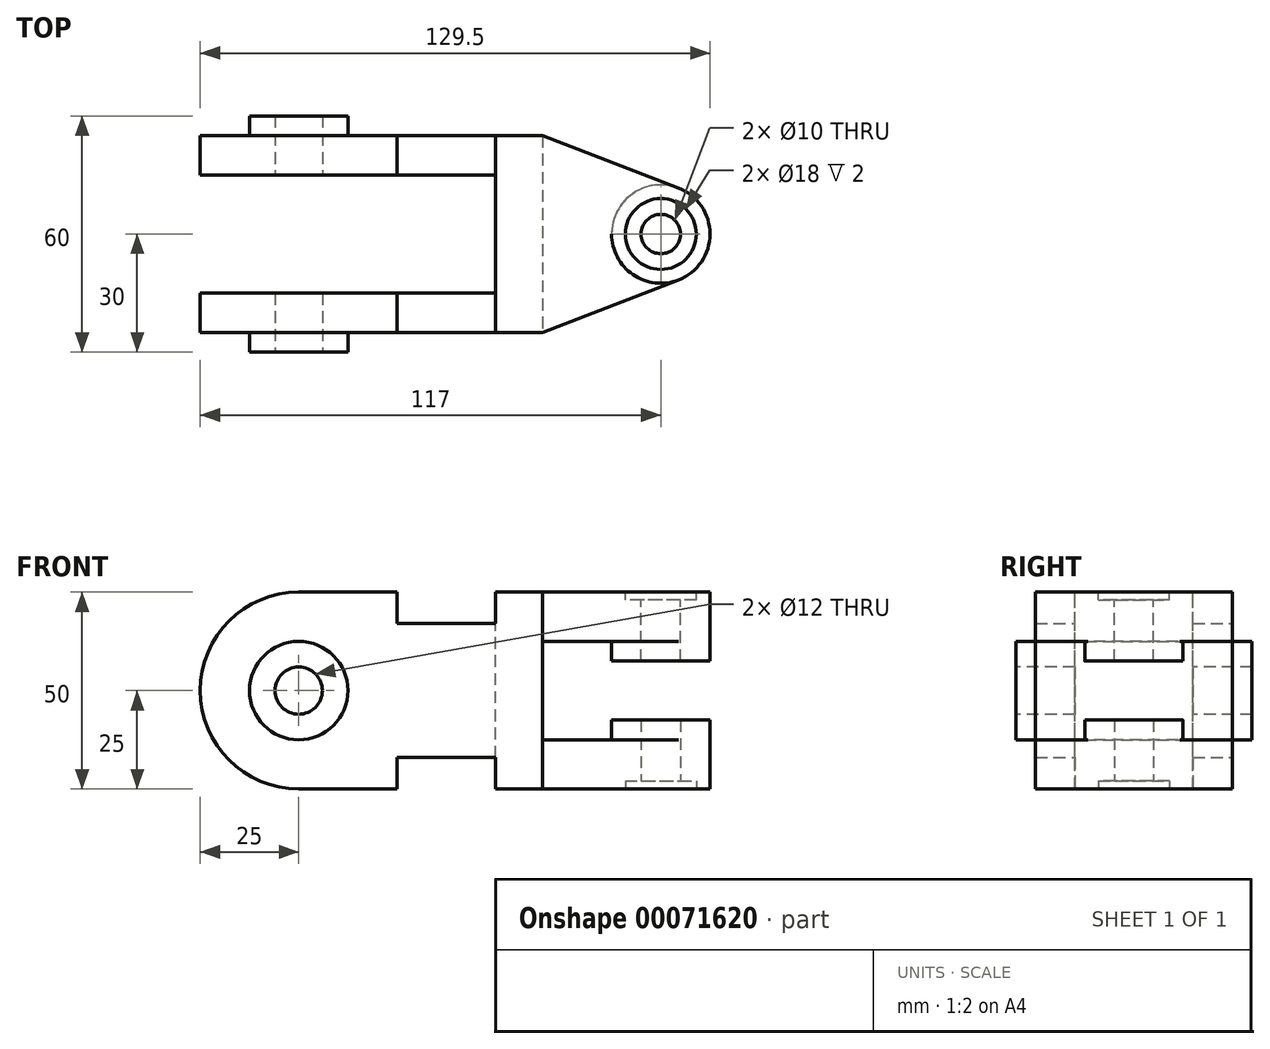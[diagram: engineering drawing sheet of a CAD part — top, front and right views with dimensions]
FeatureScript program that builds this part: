
annotation { "Feature Type Name" : "Feature", "Feature Type Description" : "" }
export const myFeature = defineFeature(function(context is Context, id is Id, definition is map)
    precondition{}
    {
        {
            var Q0;
            Q0=qCreatedBy(makeId("Front.planeOp"),FACE);
            var sketch = newSketch(context, id + "F0", { "sketchPlane" : qUnion([Q0])});
            skArc(sketch, "E0", {"start": v(0, 25) * mm, "mid": v(-25, 0) * mm, "end": v(0, -25) * mm});
            skLineSegment(sketch, "E1", {"start": v(0, 25) * mm, "end": v(25, 25) * mm});
            skLineSegment(sketch, "E2", {"start": v(25, 25) * mm, "end": v(25, 17) * mm});
            skLineSegment(sketch, "E3", {"start": v(25, 17) * mm, "end": v(50, 17) * mm});
            skLineSegment(sketch, "E4", {"start": v(50, 17) * mm, "end": v(50, 25) * mm});
            skLineSegment(sketch, "E5", {"start": v(50, 25) * mm, "end": v(62, 25) * mm});
            skLineSegment(sketch, "E6", {"start": v(62, 25) * mm, "end": v(62, 0) * mm});
            skLineSegment(sketch, "E7.MirrorCS", {"start": v(0, -25) * mm, "end": v(25, -25) * mm});
            skLineSegment(sketch, "E8.MirrorCS", {"start": v(25, -25) * mm, "end": v(25, -17) * mm});
            skLineSegment(sketch, "E9.MirrorCS", {"start": v(25, -17) * mm, "end": v(50, -17) * mm});
            skLineSegment(sketch, "E10.MirrorCS", {"start": v(50, -17) * mm, "end": v(50, -25) * mm});
            skLineSegment(sketch, "E11.MirrorCS", {"start": v(50, -25) * mm, "end": v(62, -25) * mm});
            skLineSegment(sketch, "E12.MirrorCS", {"start": v(62, -25) * mm, "end": v(62, 0) * mm});
            skSolve(sketch);
        }
        {
            var Q0;
            Q0=makeQuery(id+"F0.imprint","IMPRINT",FACE,{"disambiguationData":[TD([[makeQuery(id+"F0.imprint","IMPRINT",EDGE,{"derivedFrom":sQuery(id+"F0.wireOp",EDGE,"E0")}),1.0]])]});
            extrude(context, id + "F1", {"entities" : qUnion([Q0]), "depth" : 50 * mm});
        }
        {
            var Q0;
            Q0=makeQuery(id+"F1.opExtrude","SWEPT_FACE",FACE,{"disambiguationData":[OSD([sQuery(id+"F0.wireOp",EDGE,"E1")])]});
            var sketch = newSketch(context, id + "F2", { "sketchPlane" : qUnion([Q0])});
            skLineSegment(sketch, "E13.bottom", {"start": v(50, -10) * mm, "end": v(-25, -10) * mm});
            skLineSegment(sketch, "E13.top", {"start": v(50, -40) * mm, "end": v(-25, -40) * mm});
            skLineSegment(sketch, "E13.left", {"start": v(50, -10) * mm, "end": v(50, -40) * mm});
            skLineSegment(sketch, "E13.right", {"start": v(-25, -10) * mm, "end": v(-25, -40) * mm});
            skSolve(sketch);
        }
        {
            var Q0;
            {var subQ0=sQuery(id+"F2.wireOp",EDGE,"E13.right");Q0=makeQuery(id+"F2.imprint","IMPRINT",FACE,{"disambiguationData":[TD([[makeQuery(id+"F2.imprint","IMPRINT",EDGE,{"derivedFrom":subQ0}),1.0]])]});}
            var Q1;
            {var subQ0=sQuery(id+"F2.wireOp",EDGE,"E13.bottom");var subQ1=sQuery(id+"F0.wireOp",EDGE,"E1");var subQ2=makeQuery(id+"F1.opExtrude","SWEPT_EDGE",EDGE,{"disambiguationData":[OSD([subQ1,sQuery(id+"F0.wireOp",EDGE,"E2")])]});var subQ3=makeQuery(id+"F2.imprint","INTERSECT",VERTEX,{"derivedFrom":[subQ2,subQ0]});Q1=makeQuery(id+"F2.imprint","IMPRINT",FACE,{"disambiguationData":[TD([[makeQuery(id+"F2.imprint","IMPRINT",EDGE,{"disambiguationData":[TD([[subQ3,-1.0]])],"derivedFrom":subQ0}),1.0]])]});}
            var Q2;
            {var subQ0=sQuery(id+"F2.wireOp",EDGE,"E13.left");Q2=makeQuery(id+"F2.imprint","IMPRINT",FACE,{"disambiguationData":[TD([[makeQuery(id+"F2.imprint","IMPRINT",EDGE,{"derivedFrom":subQ0}),-1.0]])]});}
            extrude(context, id + "F3", {"entities" : qUnion([Q0, Q1, Q2]), "operationType" : NewBodyOperationType.REMOVE, "endBound" : BoundingType.THROUGH_ALL, "oppositeDirection" : true, "depth" : 25 * mm});
        }
        {
            var Q0;
            Q0=makeQuery(id+"F1.opExtrude","SWEPT_FACE",FACE,{"disambiguationData":[OSD([sQuery(id+"F0.wireOp",EDGE,"E5")])]});
            var sketch = newSketch(context, id + "F4", { "sketchPlane" : qUnion([Q0])});
            skArc(sketch, "E14", {"start": v(96.5, -36.66) * mm, "mid": v(104.5, -25) * mm, "end": v(96.5, -13.34) * mm});
            skPoint(sketch, "E14.centerSnap0", {"position": v(62, -25) * mm});
            skLineSegment(sketch, "E15", {"start": v(62, 0) * mm, "end": v(96.5, -13.34) * mm});
            skLineSegment(sketch, "E16", {"start": v(62, -50) * mm, "end": v(96.5, -36.66) * mm});
            skSolve(sketch);
        }
        {
            var Q0;
            Q0=makeQuery(id+"F4.imprint","IMPRINT",FACE,{"disambiguationData":[TD([[makeQuery(id+"F4.imprint","IMPRINT",EDGE,{"derivedFrom":sQuery(id+"F4.wireOp",EDGE,"E14")}),1.0]])]});
            extrude(context, id + "F5", {"entities" : qUnion([Q0]), "operationType" : NewBodyOperationType.ADD, "oppositeDirection" : true, "depth" : 50 * mm});
        }
        {
            var Q0;
            Q0=makeQuery(id+"F1.opExtrude","CAP_FACE",FACE,{"disambiguationData":[OSD([sQuery(id+"F0.wireOp",EDGE,"E0"),sQuery(id+"F0.wireOp",EDGE,"E1"),sQuery(id+"F0.wireOp",EDGE,"E2"),sQuery(id+"F0.wireOp",EDGE,"E3"),sQuery(id+"F0.wireOp",EDGE,"E4"),sQuery(id+"F0.wireOp",EDGE,"E5"),sQuery(id+"F0.wireOp",EDGE,"E6"),sQuery(id+"F0.wireOp",EDGE,"E7.MirrorCS"),sQuery(id+"F0.wireOp",EDGE,"E8.MirrorCS"),sQuery(id+"F0.wireOp",EDGE,"E9.MirrorCS"),sQuery(id+"F0.wireOp",EDGE,"E10.MirrorCS"),sQuery(id+"F0.wireOp",EDGE,"E11.MirrorCS"),sQuery(id+"F0.wireOp",EDGE,"E12.MirrorCS")])],"isStart":false});
            var sketch = newSketch(context, id + "F6", { "sketchPlane" : qUnion([Q0])});
            skLineSegment(sketch, "E17.bottom", {"start": v(62, -12.5) * mm, "end": v(104.5, -12.5) * mm});
            skLineSegment(sketch, "E17.top", {"start": v(62, 12.5) * mm, "end": v(104.5, 12.5) * mm});
            skLineSegment(sketch, "E17.left", {"start": v(62, -12.5) * mm, "end": v(62, 12.5) * mm});
            skLineSegment(sketch, "E17.right", {"start": v(104.5, -12.5) * mm, "end": v(104.5, 12.5) * mm});
            skSolve(sketch);
        }
        {
            var Q0;
            Q0=makeQuery(id+"F6.imprint","IMPRINT",FACE,{"disambiguationData":[TD([[makeQuery(id+"F6.imprint","IMPRINT",EDGE,{"derivedFrom":sQuery(id+"F6.wireOp",EDGE,"E17.bottom")}),1.0]])]});
            extrude(context, id + "F7", {"entities" : qUnion([Q0]), "operationType" : NewBodyOperationType.REMOVE, "endBound" : BoundingType.THROUGH_ALL, "oppositeDirection" : true, "depth" : 50 * mm});
        }
        {
            var Q0;
            Q0=makeQuery(id+"F1.opExtrude","CAP_FACE",FACE,{"disambiguationData":[OSD([sQuery(id+"F0.wireOp",EDGE,"E0"),sQuery(id+"F0.wireOp",EDGE,"E1"),sQuery(id+"F0.wireOp",EDGE,"E2"),sQuery(id+"F0.wireOp",EDGE,"E3"),sQuery(id+"F0.wireOp",EDGE,"E4"),sQuery(id+"F0.wireOp",EDGE,"E5"),sQuery(id+"F0.wireOp",EDGE,"E6"),sQuery(id+"F0.wireOp",EDGE,"E7.MirrorCS"),sQuery(id+"F0.wireOp",EDGE,"E8.MirrorCS"),sQuery(id+"F0.wireOp",EDGE,"E9.MirrorCS"),sQuery(id+"F0.wireOp",EDGE,"E10.MirrorCS"),sQuery(id+"F0.wireOp",EDGE,"E11.MirrorCS"),sQuery(id+"F0.wireOp",EDGE,"E12.MirrorCS")])],"isStart":false});
            var sketch = newSketch(context, id + "F8", { "sketchPlane" : qUnion([Q0])});
            skCircle(sketch, "E18", {"center": v(0, 0) * mm, "radius": 12.5 * mm});
            skSolve(sketch);
        }
        {
            var Q0;
            Q0=makeQuery(id+"F8.imprint","IMPRINT",FACE,{"disambiguationData":[TD([[makeQuery(id+"F8.imprint","IMPRINT",EDGE,{"derivedFrom":sQuery(id+"F8.wireOp",EDGE,"E18")}),1.0]])]});
            extrude(context, id + "F9", {"entities" : qUnion([Q0]), "operationType" : NewBodyOperationType.ADD, "depth" : 5 * mm});
        }
        {
            var Q0;
            Q0=makeQuery(id+"F1.opExtrude","CAP_FACE",FACE,{"disambiguationData":[OSD([sQuery(id+"F0.wireOp",EDGE,"E0"),sQuery(id+"F0.wireOp",EDGE,"E1"),sQuery(id+"F0.wireOp",EDGE,"E2"),sQuery(id+"F0.wireOp",EDGE,"E3"),sQuery(id+"F0.wireOp",EDGE,"E4"),sQuery(id+"F0.wireOp",EDGE,"E5"),sQuery(id+"F0.wireOp",EDGE,"E6"),sQuery(id+"F0.wireOp",EDGE,"E7.MirrorCS"),sQuery(id+"F0.wireOp",EDGE,"E8.MirrorCS"),sQuery(id+"F0.wireOp",EDGE,"E9.MirrorCS"),sQuery(id+"F0.wireOp",EDGE,"E10.MirrorCS"),sQuery(id+"F0.wireOp",EDGE,"E11.MirrorCS"),sQuery(id+"F0.wireOp",EDGE,"E12.MirrorCS")])],"isStart":true});
            var sketch = newSketch(context, id + "F10", { "sketchPlane" : qUnion([Q0])});
            skCircle(sketch, "E19", {"center": v(0, 0) * mm, "radius": 12.5 * mm});
            skSolve(sketch);
        }
        {
            var Q0;
            Q0=makeQuery(id+"F10.imprint","IMPRINT",FACE,{"disambiguationData":[TD([[makeQuery(id+"F10.imprint","IMPRINT",EDGE,{"derivedFrom":sQuery(id+"F10.wireOp",EDGE,"E19")}),1.0]])]});
            extrude(context, id + "F11", {"entities" : qUnion([Q0]), "operationType" : NewBodyOperationType.ADD, "depth" : 5 * mm});
        }
        {
            var Q0;
            Q0=makeQuery(id+"F11.opExtrude","CAP_FACE",FACE,{"disambiguationData":[OSD([sQuery(id+"F10.wireOp",EDGE,"E19")])],"isStart":false});
            var sketch = newSketch(context, id + "F12", { "sketchPlane" : qUnion([Q0])});
            skCircle(sketch, "E20", {"center": v(0, 0) * mm, "radius": 6 * mm});
            skSolve(sketch);
        }
        {
            var Q0;
            Q0=makeQuery(id+"F12.imprint","IMPRINT",FACE,{"disambiguationData":[TD([[makeQuery(id+"F12.imprint","IMPRINT",EDGE,{"derivedFrom":sQuery(id+"F12.wireOp",EDGE,"E20")}),1.0]])]});
            extrude(context, id + "F13", {"entities" : qUnion([Q0]), "operationType" : NewBodyOperationType.REMOVE, "endBound" : BoundingType.THROUGH_ALL, "depth" : 25 * mm});
        }
        {
            var Q0;
            Q0=makeQuery(id+"F9.opExtrude","CAP_FACE",FACE,{"disambiguationData":[OSD([sQuery(id+"F8.wireOp",EDGE,"E18")])],"isStart":false});
            var sketch = newSketch(context, id + "F14", { "sketchPlane" : qUnion([Q0])});
            skPoint(sketch, "E21", {"position": v(0, 0) * mm});
            skSolve(sketch);
        }
        {
            var Q0;
            Q0=sQuery(id+"F14.wireOp",VERTEX,"E21");
            var Q1;
            Q1=makeQuery(id+"F1.opExtrude","SWEPT_BODY",BODY,{"disambiguationData":[OSD([sQuery(id+"F0.wireOp",EDGE,"E0"),sQuery(id+"F0.wireOp",EDGE,"E1"),sQuery(id+"F0.wireOp",EDGE,"E2"),sQuery(id+"F0.wireOp",EDGE,"E3"),sQuery(id+"F0.wireOp",EDGE,"E4"),sQuery(id+"F0.wireOp",EDGE,"E5"),sQuery(id+"F0.wireOp",EDGE,"E6"),sQuery(id+"F0.wireOp",EDGE,"E7.MirrorCS"),sQuery(id+"F0.wireOp",EDGE,"E8.MirrorCS"),sQuery(id+"F0.wireOp",EDGE,"E9.MirrorCS"),sQuery(id+"F0.wireOp",EDGE,"E10.MirrorCS"),sQuery(id+"F0.wireOp",EDGE,"E11.MirrorCS"),sQuery(id+"F0.wireOp",EDGE,"E12.MirrorCS")])]});
            hole(context, id + "F15", {"style" : HoleStyle.SIMPLE, "holeDiameter" : 12 * mm, "endStyle" : HoleEndStyle.THROUGH, "locations" : qUnion([Q0]), "scope" : qUnion([Q1])});
        }
        {
            var Q0;
            Q0=makeQuery(id+"F7.boolean.opBoolean","COPY",FACE,{"derivedFrom":makeQuery(id+"F7.opExtrude","SWEPT_FACE",FACE,{"disambiguationData":[OSD([sQuery(id+"F6.wireOp",EDGE,"E17.bottom")])]})});
            var sketch = newSketch(context, id + "F16", { "sketchPlane" : qUnion([Q0])});
            skCircle(sketch, "E22", {"center": v(92, -25) * mm, "radius": 12.5 * mm});
            skSolve(sketch);
        }
        {
            var Q0;
            {var subQ0=sQuery(id+"F16.wireOp",EDGE,"E22");var subQ1=makeQuery(id+"F7.opExtrude","SWEPT_FACE",FACE,{"disambiguationData":[OSD([sQuery(id+"F6.wireOp",EDGE,"E17.bottom")])]});var subQ2=makeQuery(id+"F16.imprint","INTERSECT",VERTEX,{"derivedFrom":[makeQuery(id+"F7.boolean.opBoolean","INTERSECT",EDGE,{"derivedFrom":[makeQuery(id+"F5.opExtrude","SWEPT_FACE",FACE,{"disambiguationData":[OSD([sQuery(id+"F4.wireOp",EDGE,"E16")])]}),subQ1]}),subQ0]});Q0=makeQuery(id+"F16.imprint","IMPRINT",FACE,{"disambiguationData":[TD([[makeQuery(id+"F16.imprint","IMPRINT",EDGE,{"disambiguationData":[TD([[subQ2,1.0]])],"derivedFrom":subQ0}),1.0]])]});}
            extrude(context, id + "F17", {"entities" : qUnion([Q0]), "operationType" : NewBodyOperationType.ADD, "depth" : 5 * mm});
        }
        {
            var Q0;
            Q0=makeQuery(id+"F7.boolean.opBoolean","COPY",FACE,{"derivedFrom":makeQuery(id+"F7.opExtrude","SWEPT_FACE",FACE,{"disambiguationData":[OSD([sQuery(id+"F6.wireOp",EDGE,"E17.top")])]})});
            var sketch = newSketch(context, id + "F18", { "sketchPlane" : qUnion([Q0])});
            skCircle(sketch, "E23", {"center": v(92, 25) * mm, "radius": 12.5 * mm});
            skSolve(sketch);
        }
        {
            var Q0;
            {var subQ0=sQuery(id+"F18.wireOp",EDGE,"E23");Q0=makeQuery(id+"F18.imprint","IMPRINT",FACE,{"disambiguationData":[TD([[makeQuery(id+"F18.imprint","IMPRINT",EDGE,{"disambiguationData":[OD(0.0)],"derivedFrom":subQ0}),1.0]])]});}
            extrude(context, id + "F19", {"entities" : qUnion([Q0]), "operationType" : NewBodyOperationType.ADD, "depth" : 5 * mm});
        }
        {
            var Q0;
            {var subQ0=sQuery(id+"F0.wireOp",EDGE,"E5");Q0=makeQuery(id+"F5.boolean.opBoolean","MERGE",FACE,{"derivedFrom":[makeQuery(id+"F1.opExtrude","SWEPT_FACE",FACE,{"disambiguationData":[OSD([subQ0])]}),makeQuery(id+"F5.opExtrude","CAP_FACE",FACE,{"disambiguationData":[OSD([subQ0,sQuery(id+"F0.wireOp",EDGE,"E6"),sQuery(id+"F4.wireOp",EDGE,"E14"),sQuery(id+"F4.wireOp",EDGE,"E15"),sQuery(id+"F4.wireOp",EDGE,"E16")])],"isStart":true})]});}
            var sketch = newSketch(context, id + "F20", { "sketchPlane" : qUnion([Q0])});
            skPoint(sketch, "E24", {"position": v(92, -25) * mm});
            skSolve(sketch);
        }
        {
            var Q0;
            Q0=sQuery(id+"F20.wireOp",VERTEX,"E24");
            var Q1;
            Q1=makeQuery(id+"F1.opExtrude","SWEPT_BODY",BODY,{"disambiguationData":[OSD([sQuery(id+"F0.wireOp",EDGE,"E0"),sQuery(id+"F0.wireOp",EDGE,"E1"),sQuery(id+"F0.wireOp",EDGE,"E2"),sQuery(id+"F0.wireOp",EDGE,"E3"),sQuery(id+"F0.wireOp",EDGE,"E4"),sQuery(id+"F0.wireOp",EDGE,"E5"),sQuery(id+"F0.wireOp",EDGE,"E6"),sQuery(id+"F0.wireOp",EDGE,"E7.MirrorCS"),sQuery(id+"F0.wireOp",EDGE,"E8.MirrorCS"),sQuery(id+"F0.wireOp",EDGE,"E9.MirrorCS"),sQuery(id+"F0.wireOp",EDGE,"E10.MirrorCS"),sQuery(id+"F0.wireOp",EDGE,"E11.MirrorCS"),sQuery(id+"F0.wireOp",EDGE,"E12.MirrorCS")])]});
            hole(context, id + "F21", {"style" : HoleStyle.C_BORE, "holeDiameter" : 10 * mm, "cBoreDiameter" : 18 * mm, "cBoreDepth" : 2 * mm, "endStyle" : HoleEndStyle.BLIND, "holeDepth" : 17.5 * mm, "locations" : qUnion([Q0]), "scope" : qUnion([Q1])});
        }
        {
            var Q0;
            Q0=makeQuery(id+"F5.boolean.opBoolean","MERGE",FACE,{"derivedFrom":[makeQuery(id+"F1.opExtrude","SWEPT_FACE",FACE,{"disambiguationData":[OSD([sQuery(id+"F0.wireOp",EDGE,"E11.MirrorCS")])]}),makeQuery(id+"F5.opExtrude","CAP_FACE",FACE,{"disambiguationData":[OSD([sQuery(id+"F0.wireOp",EDGE,"E5"),sQuery(id+"F0.wireOp",EDGE,"E6"),sQuery(id+"F4.wireOp",EDGE,"E14"),sQuery(id+"F4.wireOp",EDGE,"E15"),sQuery(id+"F4.wireOp",EDGE,"E16")])],"isStart":false})]});
            var sketch = newSketch(context, id + "F22", { "sketchPlane" : qUnion([Q0])});
            skPoint(sketch, "E25", {"position": v(92, 25) * mm});
            skSolve(sketch);
        }
        {
            var Q0;
            Q0=sQuery(id+"F22.wireOp",VERTEX,"E25");
            var Q1;
            Q1=makeQuery(id+"F1.opExtrude","SWEPT_BODY",BODY,{"disambiguationData":[OSD([sQuery(id+"F0.wireOp",EDGE,"E0"),sQuery(id+"F0.wireOp",EDGE,"E1"),sQuery(id+"F0.wireOp",EDGE,"E2"),sQuery(id+"F0.wireOp",EDGE,"E3"),sQuery(id+"F0.wireOp",EDGE,"E4"),sQuery(id+"F0.wireOp",EDGE,"E5"),sQuery(id+"F0.wireOp",EDGE,"E6"),sQuery(id+"F0.wireOp",EDGE,"E7.MirrorCS"),sQuery(id+"F0.wireOp",EDGE,"E8.MirrorCS"),sQuery(id+"F0.wireOp",EDGE,"E9.MirrorCS"),sQuery(id+"F0.wireOp",EDGE,"E10.MirrorCS"),sQuery(id+"F0.wireOp",EDGE,"E11.MirrorCS"),sQuery(id+"F0.wireOp",EDGE,"E12.MirrorCS")])]});
            hole(context, id + "F23", {"style" : HoleStyle.C_BORE, "holeDiameter" : 10 * mm, "cBoreDiameter" : 18 * mm, "cBoreDepth" : 2 * mm, "endStyle" : HoleEndStyle.BLIND, "holeDepth" : 17.5 * mm, "locations" : qUnion([Q0]), "scope" : qUnion([Q1])});
        }
    });
